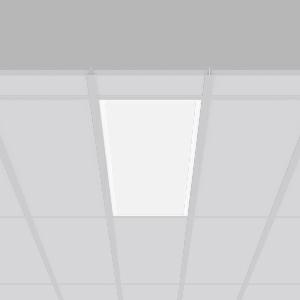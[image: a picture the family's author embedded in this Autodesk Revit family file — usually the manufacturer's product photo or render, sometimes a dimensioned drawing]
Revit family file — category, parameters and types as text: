
# Revit family: sidelite_eco_672371_002_1_04_8f7d
name_source: partatom
category: Lighting Fixtures
units: mm (PartAtom-declared; Revit-internal decimal feet)

## family parameters
Cut with Voids When Loaded = No
Host = Face
Light Source = No
Part Type = Normal
Room Calculation Point = No
Round Connector Dimension = Use Diameter
Shared = No

## types (1)
- SIDELITE ECO (1 x LED Modul 840, 3550 lm, 4000)
    Apparent Load = 29 VA
    CIE Flux Codes = 46 79 96 100 100
    Color Rendering = 80
    Color Temperature = 4000
    Default Elevation = 1800 mm
    Description = Series: SIDELITE ECO
Highly economical recessed luminaire with progressive LED technology. For escape route illumination. Frame made of aluminium, powder-coated. Diffuser: plastic, opal. Lightguide and diffuser made of non-yellowing plastic (PMMA). Lateral light emission (RZB SIDELITE technology) for homogeneous light distribution. External driver. Self-contained system with automatic self-test and feedback to the RZB monitoring system MULTIDIGIT. External driver with simple plug-in locking system. Extended connection cable (1.90 m). 
Colour: white
Length: 1195 mm
Width: 295 mm
Cut-out length: 1170 mm
Cut-out width: 270 mm
Recess height: 160 mm
Luminaire: recess height: 40 mm
Weight: 4.42 kg
Operating mode: maintained power mode
Duration time: 3 h
Lamp: LED
Socket: without socket
Colour temperature: 4000K
Colour rendering index (CRI): 80
System power: 29 W
Rated luminous flux: 3550 lm
Luminous flux, emergency: 520 lm
System power, emergency: -
Control gear: Regulated power supply
Protection class: I
Type of protection: IP 40
    Height = 0 mm  [stored 0 ft]
    Lamp = 1 x LED Modul 840
    Lamp Light Flux = 3550 lm
    Lamp count = 1
    Length = 1195 mm
    Lifetime = 50000 h
    Luminous efficacy = 122 lm/W
    Manufacturer = RZB
    ModVariant = No
    Model = 672371.002.1.04
    Mounting Place = Ceiling
    Mounting Type = Recessed
    Number of Poles = 1
    OnlyDefault = Yes
    Power Factor = 1
    Product Name = SIDELITE ECO
    Product group = Recessed modular luminaires
    ProductGroupID = 406
    Protection Class = Protection class I
    Protection Degree = IP 40
    RLX_Detail_Level = 1
    RLX_Emergency_Light_Flux = 520 lm
    RLX_Emergency_Type = 3
    RLX_Emergency_Type_DB = Yes
    RlxData = <blob elided: 30737 chars, md5=f01f656d>
    Socket = socket
    Standby Power = 0 W
    System Light Flux = 3550 lm
    System Power = 29 W
    Type Comments = Product without accessories
    Type Image = 312365.002.jpg
    URL = http://relux.com
    VarID = ---
    Voltage = 230 V
    Voltage Range = 220-240 V
    Weight = 0.00 kg
    Width = 295 mm

note: [stored X ft] marks values corroborated as IEEE doubles in the binary element streams (Revit-internal decimal feet)

## geometry (parser evidence)
native form markers: Blend x4, Sweep x11
no freeform markers — native parametric forms only
